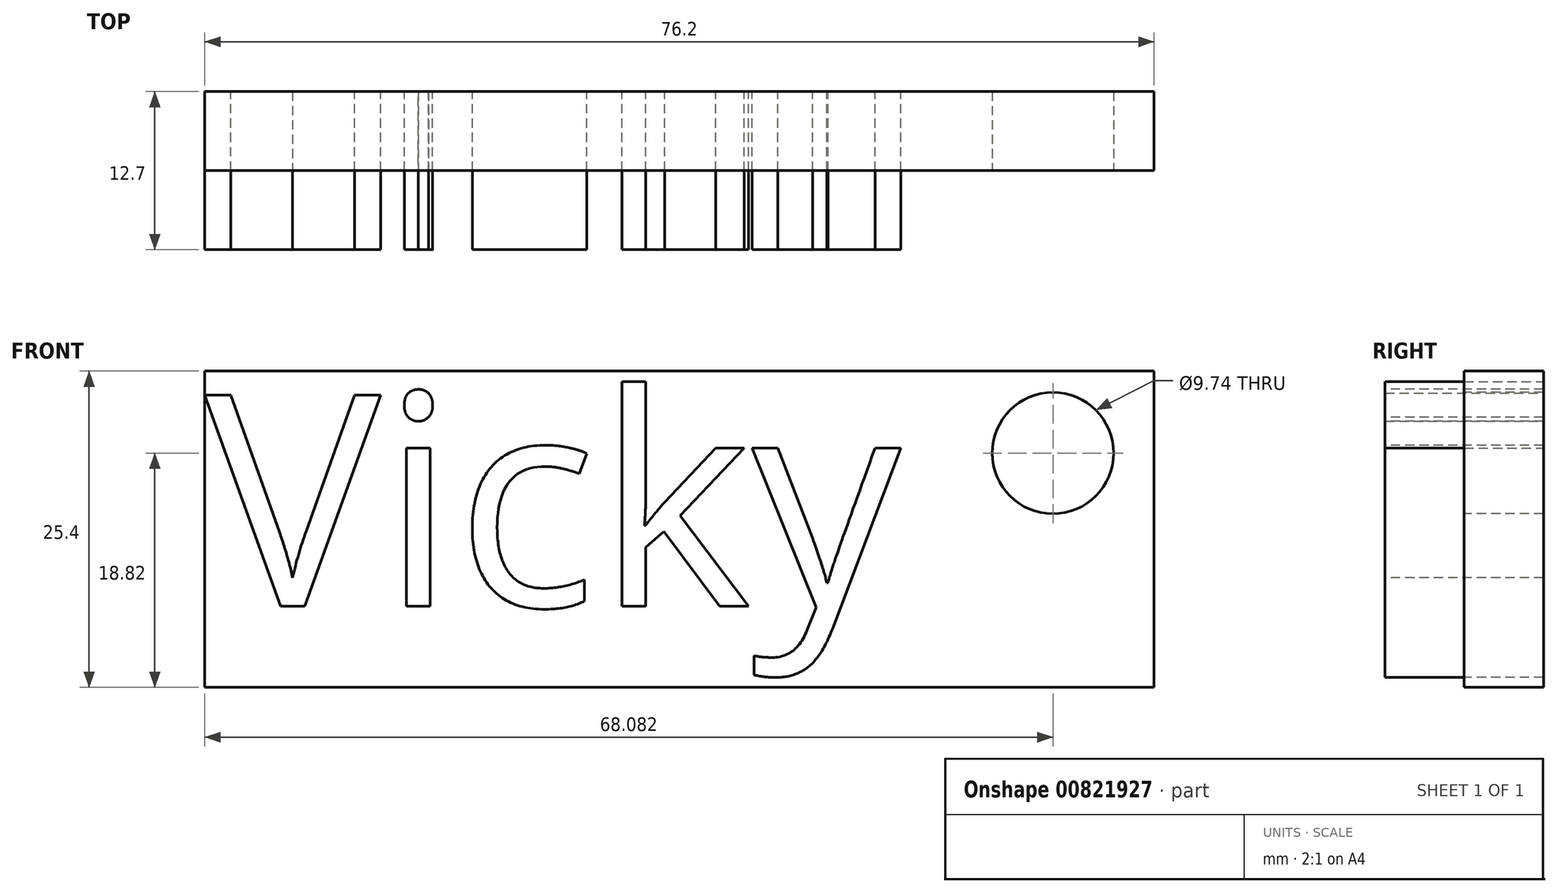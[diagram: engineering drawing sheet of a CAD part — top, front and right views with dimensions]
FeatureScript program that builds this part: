
annotation { "Feature Type Name" : "Feature", "Feature Type Description" : "" }
export const myFeature = defineFeature(function(context is Context, id is Id, definition is map)
    precondition{}
    {
        {
            var Q0;
            Q0=qCreatedBy(makeId("Front.planeOp"),FACE);
            var sketch = newSketch(context, id + "F0", { "sketchPlane" : qUnion([Q0])});
            skLineSegment(sketch, "E0", {"start": v(0, 0) * mm, "end": v(76.2, 0) * mm});
            skLineSegment(sketch, "E1", {"start": v(0, 0) * mm, "end": v(0, 25.4) * mm});
            skLineSegment(sketch, "E2", {"start": v(0, 25.4) * mm, "end": v(76.2, 25.4) * mm});
            skLineSegment(sketch, "E3", {"start": v(76.2, 25.4) * mm, "end": v(76.2, 0) * mm});
            skSolve(sketch);
        }
        {
            var Q0;
            Q0=makeQuery(id+"F0.imprint","IMPRINT",FACE,{"disambiguationData":[TD([[makeQuery(id+"F0.imprint","IMPRINT",EDGE,{"derivedFrom":sQuery(id+"F0.wireOp",EDGE,"E0")}),1.0]])]});
            var sketch = newSketch(context, id + "F1", { "sketchPlane" : qUnion([Q0])});
            skText(sketch, "E4", { "text": "Vicky", "fontName": "OpenSans-Regular.ttf"});
            const initialGuessF1  = {"E4": [0, 0.00651, 1, 0, 0.0171]};
            skSetInitialGuess(sketch, initialGuessF1);
            skSolve(sketch);
        }
        {
            var Q0;
            Q0 = qSketchRegion(id + "F1", true);
            extrude(context, id + "F2", {"entities" : qUnion([Q0]), "depth" : 12.7 * mm, "offsetDistance" : 25.4 * mm});
        }
        {
            var Q0;
            Q0=makeQuery(id+"F0.imprint","IMPRINT",FACE,{"disambiguationData":[TD([[makeQuery(id+"F0.imprint","IMPRINT",EDGE,{"derivedFrom":sQuery(id+"F0.wireOp",EDGE,"E0")}),1.0]])]});
            extrude(context, id + "F3", {"entities" : qUnion([Q0]), "depth" : 6.35 * mm, "offsetDistance" : 25.4 * mm});
        }
        {
            var Q0;
            Q0=makeQuery(id+"F3.opExtrude","CAP_FACE",FACE,{"disambiguationData":[OSD([sQuery(id+"F0.wireOp",EDGE,"E0"),sQuery(id+"F0.wireOp",EDGE,"E1"),sQuery(id+"F0.wireOp",EDGE,"E2"),sQuery(id+"F0.wireOp",EDGE,"E3")])],"isStart":false});
            var sketch = newSketch(context, id + "F4", { "sketchPlane" : qUnion([Q0])});
            skCircle(sketch, "E5", {"center": v(68.08, 18.82) * mm, "radius": 4.87 * mm});
            skSolve(sketch);
        }
        {
            var Q0;
            Q0 = qSketchRegion(id + "F4", true);
            extrude(context, id + "F5", {"entities" : qUnion([Q0]), "operationType" : NewBodyOperationType.REMOVE, "endBound" : BoundingType.UP_TO_NEXT, "oppositeDirection" : true, "depth" : 25.4 * mm, "offsetDistance" : 25.4 * mm});
        }
    });
